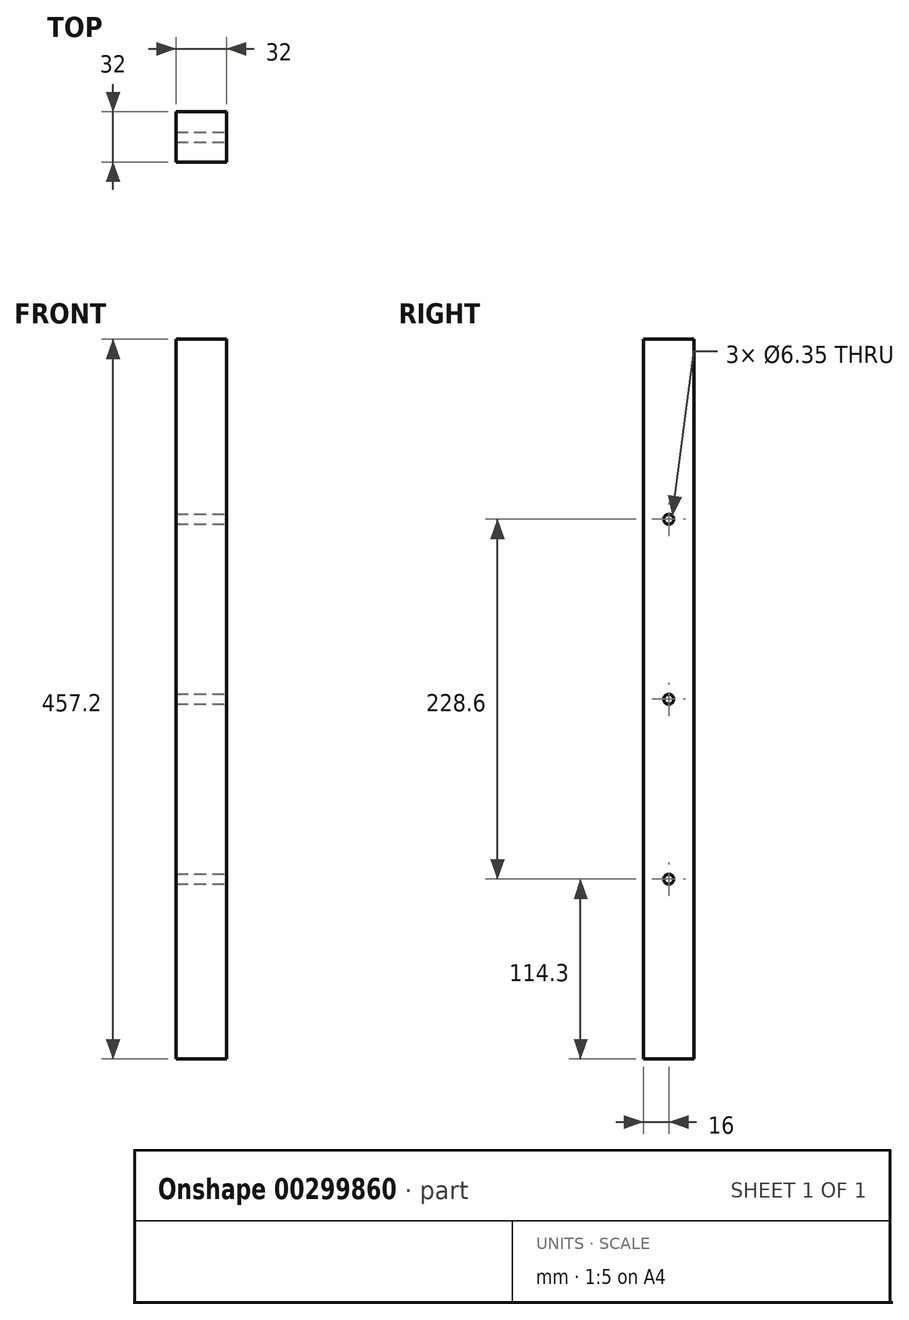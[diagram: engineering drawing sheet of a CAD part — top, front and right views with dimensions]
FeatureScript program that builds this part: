
annotation { "Feature Type Name" : "Feature", "Feature Type Description" : "" }
export const myFeature = defineFeature(function(context is Context, id is Id, definition is map)
    precondition{}
    {
        {
            var Q0;
            Q0=qCreatedBy(makeId("Top.planeOp"),FACE);
            var sketch = newSketch(context, id + "F0", { "sketchPlane" : qUnion([Q0])});
            skLineSegment(sketch, "E0.bottom", {"start": v(-16, -16) * mm, "end": v(16, -16) * mm});
            skLineSegment(sketch, "E0.top", {"start": v(-16, 16) * mm, "end": v(16, 16) * mm});
            skLineSegment(sketch, "E0.left", {"start": v(-16, -16) * mm, "end": v(-16, 16) * mm});
            skLineSegment(sketch, "E0.right", {"start": v(16, -16) * mm, "end": v(16, 16) * mm});
            skPoint(sketch, "E0.middle", {"position": v(0, 0) * mm});
            skSolve(sketch);
        }
        {
            var Q0;
            Q0=qSketchRegion(id+"F0",true);
            extrude(context, id + "F1", {"entities" : qUnion([Q0]), "depth" : 457.2 * mm});
        }
        {
            var Q0;
            Q0=makeQuery(id+"F1.opExtrude","SWEPT_FACE",FACE,{"disambiguationData":[OSD([sQuery(id+"F0.wireOp",EDGE,"E0.right")])]});
            var sketch = newSketch(context, id + "F2", { "sketchPlane" : qUnion([Q0])});
            skLineSegment(sketch, "E1", {"start": v(0, 0) * mm, "end": v(0, 114.3) * mm});
            skPoint(sketch, "E1.endSnap0", {"position": v(0, 0) * mm});
            skLineSegment(sketch, "E2", {"start": v(0, 114.3) * mm, "end": v(0, 228.6) * mm});
            skCircle(sketch, "E3", {"center": v(0, 228.6) * mm, "radius": 3.18 * mm});
            skCircle(sketch, "E4", {"center": v(0, 114.3) * mm, "radius": 3.18 * mm});
            skLineSegment(sketch, "E5", {"start": v(0, 228.6) * mm, "end": v(0, 342.9) * mm});
            skCircle(sketch, "E6", {"center": v(0, 342.9) * mm, "radius": 3.18 * mm});
            skSolve(sketch);
        }
        {
            var Q0;
            Q0=qSketchRegion(id+"F2",true);
            extrude(context, id + "F3", {"entities" : qUnion([Q0]), "operationType" : NewBodyOperationType.REMOVE, "endBound" : BoundingType.THROUGH_ALL, "oppositeDirection" : true, "depth" : 25 * mm});
        }
    });
